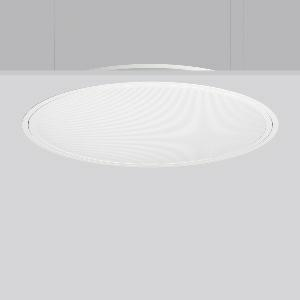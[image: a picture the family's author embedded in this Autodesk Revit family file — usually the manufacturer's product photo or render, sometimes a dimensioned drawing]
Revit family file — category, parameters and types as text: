
# Revit family: triona_round_e_312299_002_2_12_129b
name_source: partatom
category: Lighting Fixtures
units: mm (PartAtom-declared; Revit-internal decimal feet)

## family parameters
Cut with Voids When Loaded = No
Host = Face
Light Source = No
Part Type = Normal
Room Calculation Point = No
Round Connector Dimension = Use Diameter
Shared = No

## types (1)
- TuneableWhite 846 (1 x LED Modul 846, 5050 lm, 4600)
    Apparent Load = 49 VA
    CIE Flux Codes = 58 86 97 100 100
    Color Rendering = 80
    Color Temperature = 4600
    Default Elevation = 1800 mm
    Description = Series: TRIONA round
Decorative round LED recessed surface luminaire. Cover made of sheet steel, powder-coated. Frame made of aluminium, powder-coated. Recessed ring: aluminium extrusion profile, powder coated. Light emission through a diffuser in plastic, opal/prismatic. Lightguide and diffuser made of non-yellowing plastic (PMMA). Lateral light emission (RZB SIDELITE technology) for above-average homogeneous light distribution. Tunable white versions, dynamically adjustable from 2700 K to 6500 K. Suitable for installation in cavity ceilings. Tool-free mounting system thanks to the rocker arm mechanism (patent pending). Electronic ballast included. Very easy installation thanks to Plug+Play connection. Ideal for use as part of the Human Centric Lighting concept in connection with RZB light management systems. 
Colour: traffic white, matt (RAL 9016)
Diameter: 889 mm
Height: 2 mm
Cut-out diameter: 866 mm
Recess height: 100 mm
Luminaire: recess height: 89 mm
Lamp: LED
Socket: without socket
Colour temperature: 2700K - 6500K
Colour rendering index (CRI): 80
System power: 49 W
Rated luminous flux: 5050 lm
Luminous efficiency: 103 lm/W
System power 2: 51 W
Rated luminous flux 2: 4800 lm
Luminous efficiency 2: 94 lm/W
System power 3: 51 W
Rated luminous flux 3: 4900 lm
Luminous efficiency 3: 96 lm/W
Control gear: Converter, dimmable, DALI
Protection class: I
Type of protection: IP 40
    Height = 0 mm  [stored 0 ft]
    Lamp = 1 x LED Modul 846
    Lamp Light Flux = 5050 lm
    Lamp count = 1
    Length = 889 mm
    Lifetime = 50000 h
    Luminous efficacy = 103 lm/W
    Manufacturer = RZB
    ModVariant = No
    Model = 312299.002.2.12
    Mounting Place = Ceiling
    Mounting Type = Recessed
    Number of Poles = 1
    OnlyDefault = Yes
    Power Factor = 1
    Product Name = TRIONA round E
    Product group = Recessed modular luminaires
    ProductGroupID = 406
    Protection Class = Protection class I
    Protection Degree = IP 20
    RLX_Detail_Level = 1
    RLX_Emergency_Light_Flux = 0 lm
    RLX_Emergency_Type = 0
    RLX_Emergency_Type_DB = No
    RlxData = <blob elided: 40701 chars, md5=9eccc6ea>
    Socket = socket
    Standby Power = 0 W
    System Light Flux = 5050 lm
    System Power = 49 W
    Type Comments = TuneableWhite 846
    Type Image = 312299.002.12.jpg
    URL = http://relux.com
    VarID = tuneablewhite_846
    Voltage = 230 V
    Voltage Range = 220-240 V
    Weight = 0.00 kg
    Width = 0 mm  [stored 0 ft]

note: [stored X ft] marks values corroborated as IEEE doubles in the binary element streams (Revit-internal decimal feet)

## geometry (parser evidence)
native form markers: Blend x4, Sweep x10
no freeform markers — native parametric forms only
